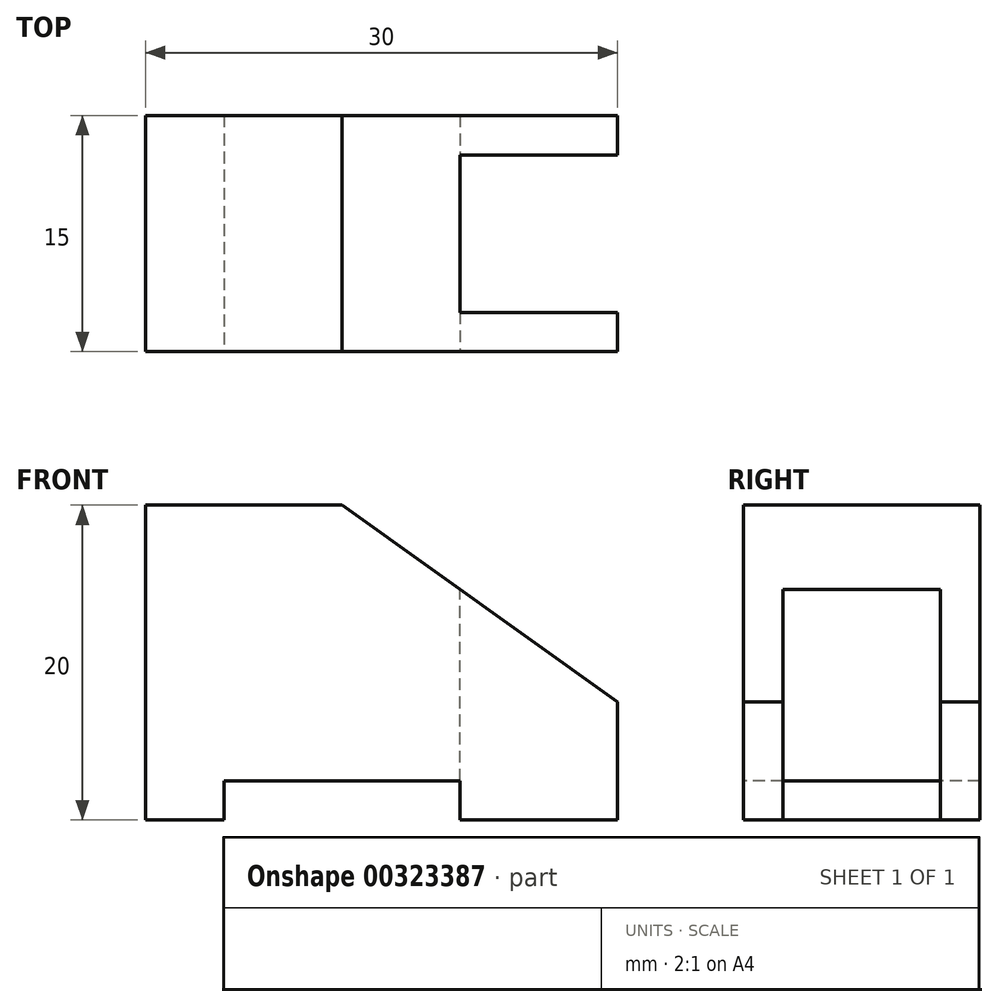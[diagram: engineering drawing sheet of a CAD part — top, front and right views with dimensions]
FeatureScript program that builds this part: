
annotation { "Feature Type Name" : "Feature", "Feature Type Description" : "" }
export const myFeature = defineFeature(function(context is Context, id is Id, definition is map)
    precondition{}
    {
        {
            var Q0;
            Q0=qCreatedBy(makeId("Front.planeOp"),FACE);
            var sketch = newSketch(context, id + "F0", { "sketchPlane" : qUnion([Q0])});
            skLineSegment(sketch, "E0", {"start": v(0, 0) * mm, "end": v(30, 0) * mm});
            skLineSegment(sketch, "E1", {"start": v(0, 0) * mm, "end": v(0, 20) * mm});
            skLineSegment(sketch, "E2", {"start": v(0, 20) * mm, "end": v(12.5, 20) * mm});
            skLineSegment(sketch, "E3", {"start": v(30, 0) * mm, "end": v(30, 7.5) * mm});
            skLineSegment(sketch, "E4", {"start": v(12.5, 20) * mm, "end": v(30, 7.5) * mm});
            skSolve(sketch);
        }
        {
            var Q0;
            Q0 = qSketchRegion(id + "F0", true);
            extrude(context, id + "F1", {"entities" : qUnion([Q0]), "endBound" : BoundingType.SYMMETRIC, "depth" : 15 * mm});
        }
        {
            var Q0;
            Q0=makeQuery(id+"F1.opExtrude","CAP_FACE",FACE,{"disambiguationData":[OSD([sQuery(id+"F0.wireOp",EDGE,"E0"),sQuery(id+"F0.wireOp",EDGE,"E1"),sQuery(id+"F0.wireOp",EDGE,"E2"),sQuery(id+"F0.wireOp",EDGE,"E3"),sQuery(id+"F0.wireOp",EDGE,"E4")])],"isStart":false});
            var sketch = newSketch(context, id + "F2", { "sketchPlane" : qUnion([Q0])});
            skLineSegment(sketch, "E5", {"start": v(5, 0) * mm, "end": v(5, 2.5) * mm});
            skLineSegment(sketch, "E6", {"start": v(5, 2.5) * mm, "end": v(20, 2.5) * mm});
            skLineSegment(sketch, "E7", {"start": v(20, 2.5) * mm, "end": v(20, 0) * mm});
            skLineSegment(sketch, "E8", {"start": v(5, 0) * mm, "end": v(20, 0) * mm});
            skLineSegment(sketch, "E9", {"start": v(5, 0) * mm, "end": v(0, 0) * mm, "construction": true});
            skLineSegment(sketch, "E10", {"start": v(20, 0) * mm, "end": v(30, 0) * mm, "construction": true});
            skSolve(sketch);
        }
        {
            var Q0;
            Q0 = qSketchRegion(id + "F2", true);
            extrude(context, id + "F3", {"entities" : qUnion([Q0]), "operationType" : NewBodyOperationType.REMOVE, "oppositeDirection" : true, "depth" : 25 * mm});
        }
        {
            var Q0;
            Q0=makeQuery(id+"F1.opExtrude","SWEPT_FACE",FACE,{"disambiguationData":[OSD([sQuery(id+"F0.wireOp",EDGE,"E2")])]});
            var sketch = newSketch(context, id + "F4", { "sketchPlane" : qUnion([Q0])});
            skLineSegment(sketch, "E11", {"start": v(19.98, 5) * mm, "end": v(19.98, -5) * mm});
            skLineSegment(sketch, "E12", {"start": v(30.98, 5) * mm, "end": v(19.98, 5) * mm});
            skLineSegment(sketch, "E13", {"start": v(19.98, -5) * mm, "end": v(30.98, -5) * mm});
            skLineSegment(sketch, "E14", {"start": v(30.98, 5) * mm, "end": v(30.98, -5) * mm});
            skSolve(sketch);
        }
        {
            var Q0;
            Q0 = qSketchRegion(id + "F4", true);
            extrude(context, id + "F5", {"entities" : qUnion([Q0]), "operationType" : NewBodyOperationType.REMOVE, "oppositeDirection" : true, "depth" : 25 * mm});
        }
        {
            var Q0;
            Q0 = qSketchRegion(id + "F4", true);
            extrude(context, id + "F6", {"entities" : qUnion([Q0]), "operationType" : NewBodyOperationType.REMOVE, "oppositeDirection" : true, "depth" : 25 * mm});
        }
    });
